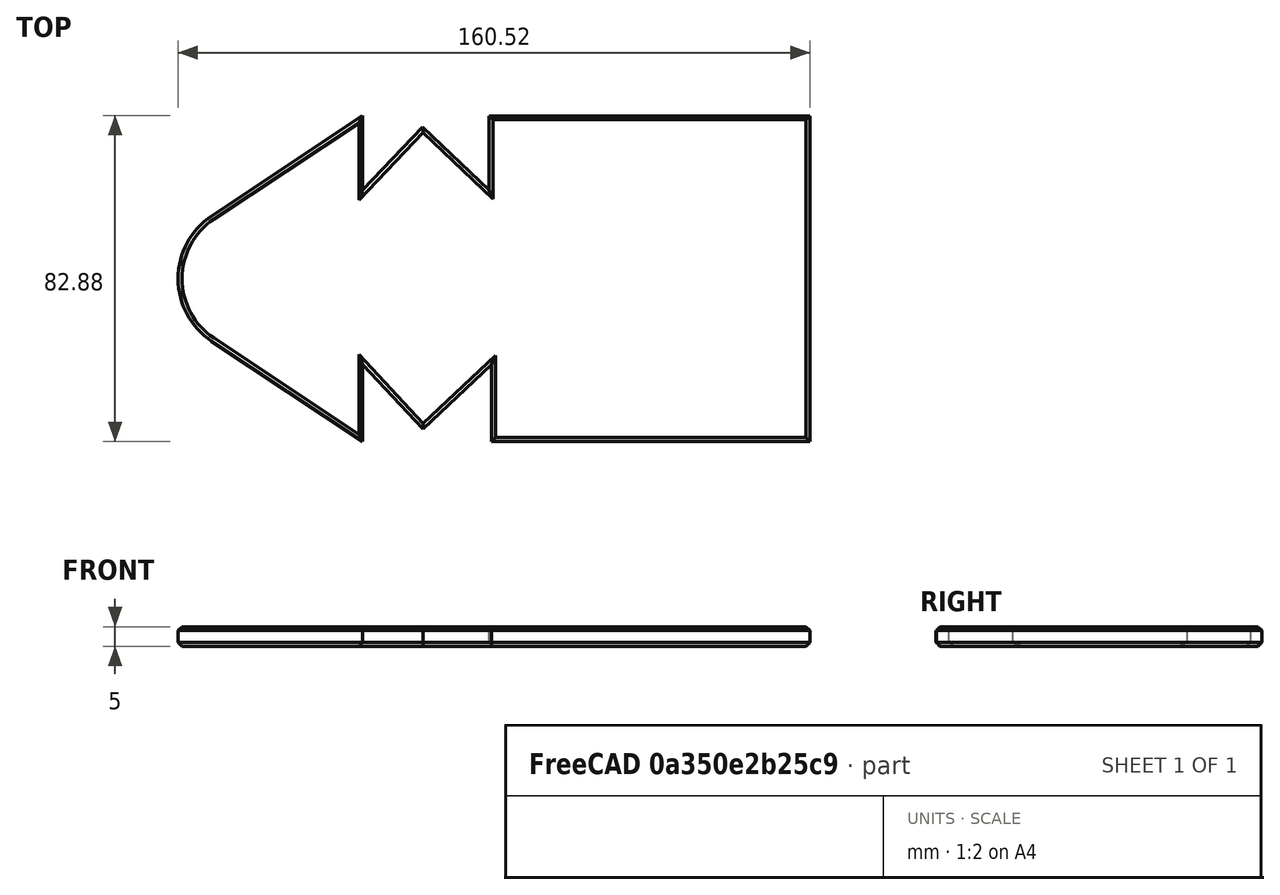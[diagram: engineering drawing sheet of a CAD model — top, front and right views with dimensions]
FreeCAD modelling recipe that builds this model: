
FCSTD DOCUMENT  (FreeCAD 0.16R6712 (Git))
Label: 1
License: All rights reserved
LicenseURL: http://en.wikipedia.org/wiki/All_rights_reserved
objects: Sketcher::SketchObject×2, Part::Chamfer×2, PartDesign::Pad×1
note: 6 computed .brp shape members not serialized (recipe doc carries the construction recipe); baked Part::Feature solids carry a one-line shape summary decoded from their .brp

FEATURE [Sketcher::SketchObject] Sketch
  sketch-geometry (14):
    g0: LineSegment StartX=57.783 StartY=41.3504 StartZ=0 EndX=57.783 EndY=-41.3504 EndZ=0
    g1: LineSegment StartX=-55.8201 StartY=41.4386 StartZ=0 EndX=-94.1851 EndY=15.9529 EndZ=0
    g2: LineSegment StartX=-55.8201 StartY=-41.4386 StartZ=0 EndX=-94.1851 EndY=-15.9529 EndZ=0
    g3: ArcOfCircle CenterX=-83.5876 CenterY=0 CenterZ=0 NormalX=0 NormalY=0 NormalZ=1 Radius=19.1521 StartAngle=2.15715 EndAngle=4.12603
    g4: LineSegment StartX=-55.8201 StartY=41.4386 StartZ=0 EndX=-55.8201 EndY=22.4996 EndZ=0
    g5: LineSegment StartX=-23.6927 StartY=22.4996 StartZ=0 EndX=-23.6927 EndY=41.3504 EndZ=0
    g6: LineSegment StartX=-23.6927 StartY=41.3504 StartZ=0 EndX=57.783 EndY=41.3504 EndZ=0
    g7: LineSegment StartX=-55.8201 StartY=22.4996 StartZ=0 EndX=-40.5842 EndY=38.5419 EndZ=0
    g8: LineSegment StartX=-40.5842 StartY=38.5419 StartZ=0 EndX=-23.6927 EndY=22.4996 EndZ=0
    g9: LineSegment StartX=-55.8201 StartY=-41.4386 StartZ=0 EndX=-55.8201 EndY=-21.8542 EndZ=0
    g10: LineSegment StartX=-23.1354 StartY=-21.8542 StartZ=0 EndX=-23.1354 EndY=-41.3504 EndZ=0
    g11: LineSegment StartX=-23.1354 StartY=-41.3504 StartZ=0 EndX=57.783 EndY=-41.3504 EndZ=0
    g12: LineSegment StartX=-55.8201 StartY=-21.8542 StartZ=0 EndX=-40.5575 EndY=-38.1608 EndZ=0
    g13: LineSegment StartX=-40.5575 StartY=-38.1608 StartZ=0 EndX=-23.1354 EndY=-21.8542 EndZ=0
  constraints (19):
    c: Vertical(g0)
    c: Tangent(g1,g3) = -1.5708
    c: Tangent(g2,g3) = 1.5708
    c: Vertical(g5)
    c: Coincident(g5,g6)
    c: Coincident(g6,g0)
    c: Horizontal(g6)
    c: Coincident(g4,g7)
    c: Coincident(g7,g8)
    c: Angle(g7,g8) = 1.5708
    c: Vertical(g10)
    c: Coincident(g10,g11)
    c: Coincident(g11,g0)
    c: Horizontal(g11)
    c: Coincident(g9,g12)
    c: Coincident(g12,g13)
    c: Angle(g13,g12) = 1.5708
    c: Symmetric(g0,g0,g-1)
    c: Symmetric(g4,g9,g-1)
FEATURE [PartDesign::Pad] Pad
  Length = 5
  Length2 = 100
  Sketch = -> Sketch
  Type = 0
FEATURE [Part::Chamfer] Chamfer
  Base = -> Pad
  Edges = 14 edges r=1: [Edge4,Edge7,Edge10,Edge13,Edge16,Edge19,Edge22,Edge25,Edge28,Edge31,Edge34,Edge37,Edge40,Edge42]
FEATURE [Part::Chamfer] Chamfer001
  Base = -> Chamfer
  Edges = 13 edges r=1: [Edge3,Edge6,Edge11,Edge12,Edge13,Edge14,Edge15,Edge16,Edge18,Edge19,Edge20,Edge21,Edge22]
FEATURE [Sketcher::SketchObject] Sketch001
  Placement = pos=(0,0,5) rot=(0,0,1;0rad)
  Support = -> Chamfer001 [Face11]
  sketch-geometry (2):
    g0: Circle CenterX=51.0641 CenterY=34.711 CenterZ=0 NormalX=0 NormalY=0 NormalZ=1 Radius=2
    g1: Circle CenterX=52.3424 CenterY=-32.9576 CenterZ=0 NormalX=0 NormalY=0 NormalZ=1 Radius=2
  constraints (2):
    c: Radius(g0) = 2
    c: Equal(g0,g1) = 2
